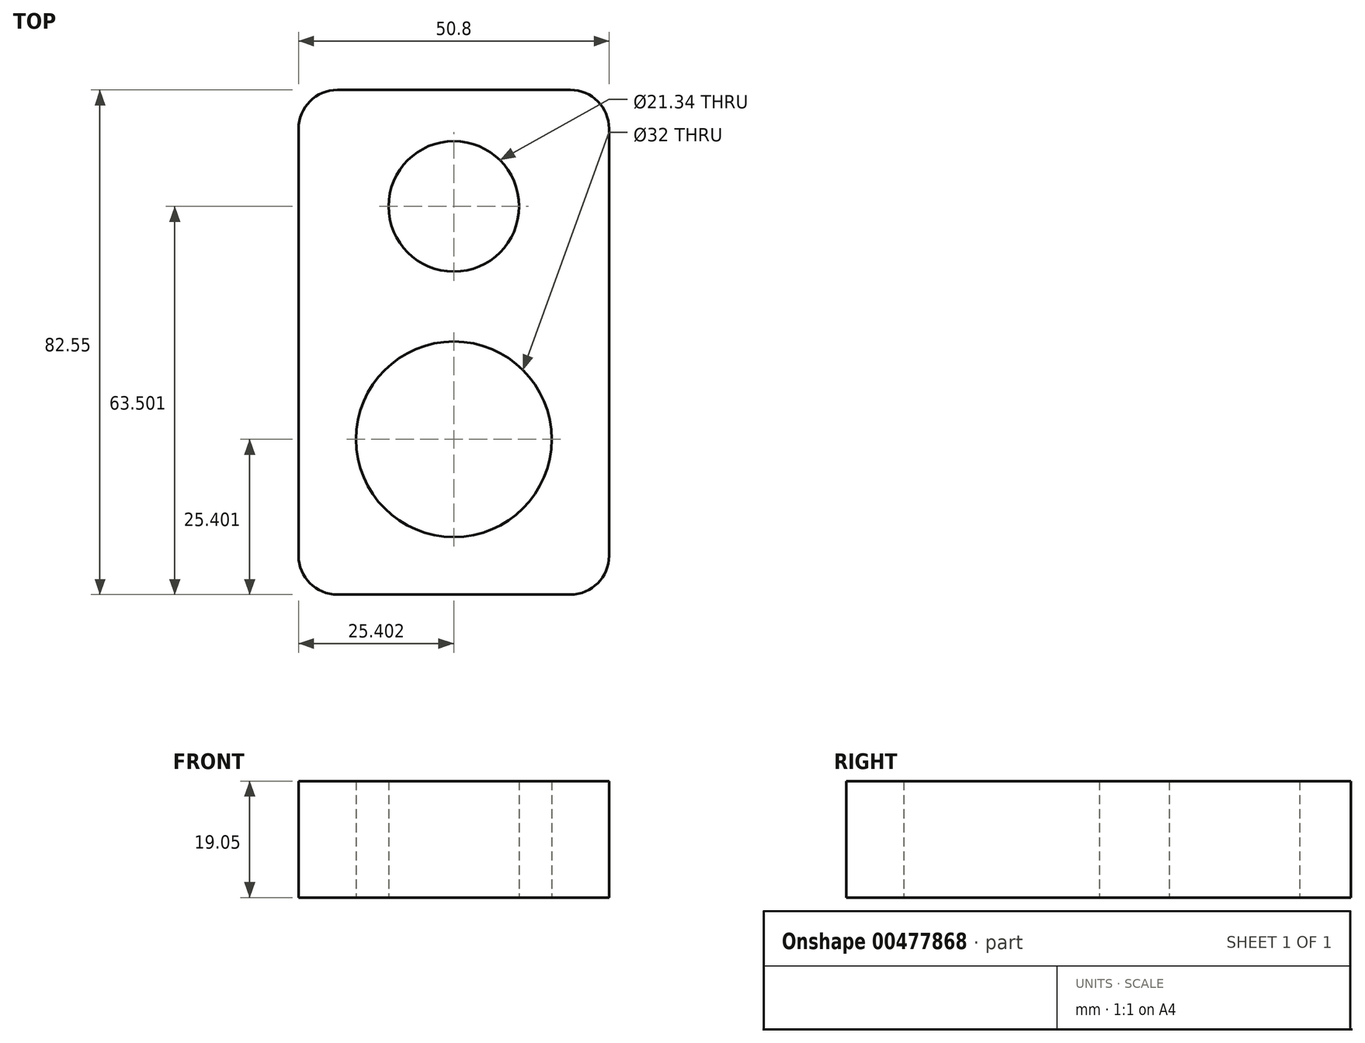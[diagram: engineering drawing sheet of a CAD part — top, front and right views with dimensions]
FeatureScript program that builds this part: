
annotation { "Feature Type Name" : "Feature", "Feature Type Description" : "" }
export const myFeature = defineFeature(function(context is Context, id is Id, definition is map)
    precondition{}
    {
        {
            var Q0;
            Q0=qCreatedBy(makeId("Top.planeOp"),FACE);
            var sketch = newSketch(context, id + "F0", { "sketchPlane" : qUnion([Q0])});
            skLineSegment(sketch, "E0.bottom", {"start": v(-69.03, -0.98) * mm, "end": v(-18.23, -0.98) * mm});
            skLineSegment(sketch, "E0.top", {"start": v(-69.03, 81.57) * mm, "end": v(-18.23, 81.57) * mm});
            skLineSegment(sketch, "E0.left", {"start": v(-69.03, -0.98) * mm, "end": v(-69.03, 81.57) * mm});
            skLineSegment(sketch, "E0.right", {"start": v(-18.23, -0.98) * mm, "end": v(-18.23, 81.57) * mm});
            skLineSegment(sketch, "E1", {"start": v(-43.63, 81.57) * mm, "end": v(-43.63, -0.98) * mm, "construction": true});
            skCircle(sketch, "E2", {"center": v(-43.63, 62.52) * mm, "radius": 10.67 * mm});
            skCircle(sketch, "E3", {"center": v(-43.63, 24.42) * mm, "radius": 16 * mm});
            skSolve(sketch);
        }
        {
            var Q0;
            Q0=makeQuery(id+"F0.imprint","IMPRINT",FACE,{"disambiguationData":[TD([[makeQuery(id+"F0.imprint","IMPRINT",EDGE,{"derivedFrom":sQuery(id+"F0.wireOp",EDGE,"E0.bottom")}),1.0]])]});
            extrude(context, id + "F1", {"entities" : qUnion([Q0]), "depth" : 19.05 * mm, "offsetDistance" : 25.4 * mm});
        }
        {
            var Q0;
            Q0=makeQuery(id+"F1.opExtrude","SWEPT_EDGE",EDGE,{"disambiguationData":[OSD([sQuery(id+"F0.wireOp",EDGE,"E0.top"),sQuery(id+"F0.wireOp",EDGE,"E0.right")])]});
            var Q1;
            Q1=makeQuery(id+"F1.opExtrude","SWEPT_EDGE",EDGE,{"disambiguationData":[OSD([sQuery(id+"F0.wireOp",EDGE,"E0.top"),sQuery(id+"F0.wireOp",EDGE,"E0.left")])]});
            var Q2;
            Q2=makeQuery(id+"F1.opExtrude","SWEPT_EDGE",EDGE,{"disambiguationData":[OSD([sQuery(id+"F0.wireOp",EDGE,"E0.bottom"),sQuery(id+"F0.wireOp",EDGE,"E0.right")])]});
            var Q3;
            Q3=makeQuery(id+"F1.opExtrude","SWEPT_EDGE",EDGE,{"disambiguationData":[OSD([sQuery(id+"F0.wireOp",EDGE,"E0.bottom"),sQuery(id+"F0.wireOp",EDGE,"E0.left")])]});
            fillet(context, id + "F2", {"entities" : qUnion([Q0, Q1, Q2, Q3]), "radius" : 6.35 * mm, "tangentPropagation" : true, "allowEdgeOverflow" : false});
        }
    });
